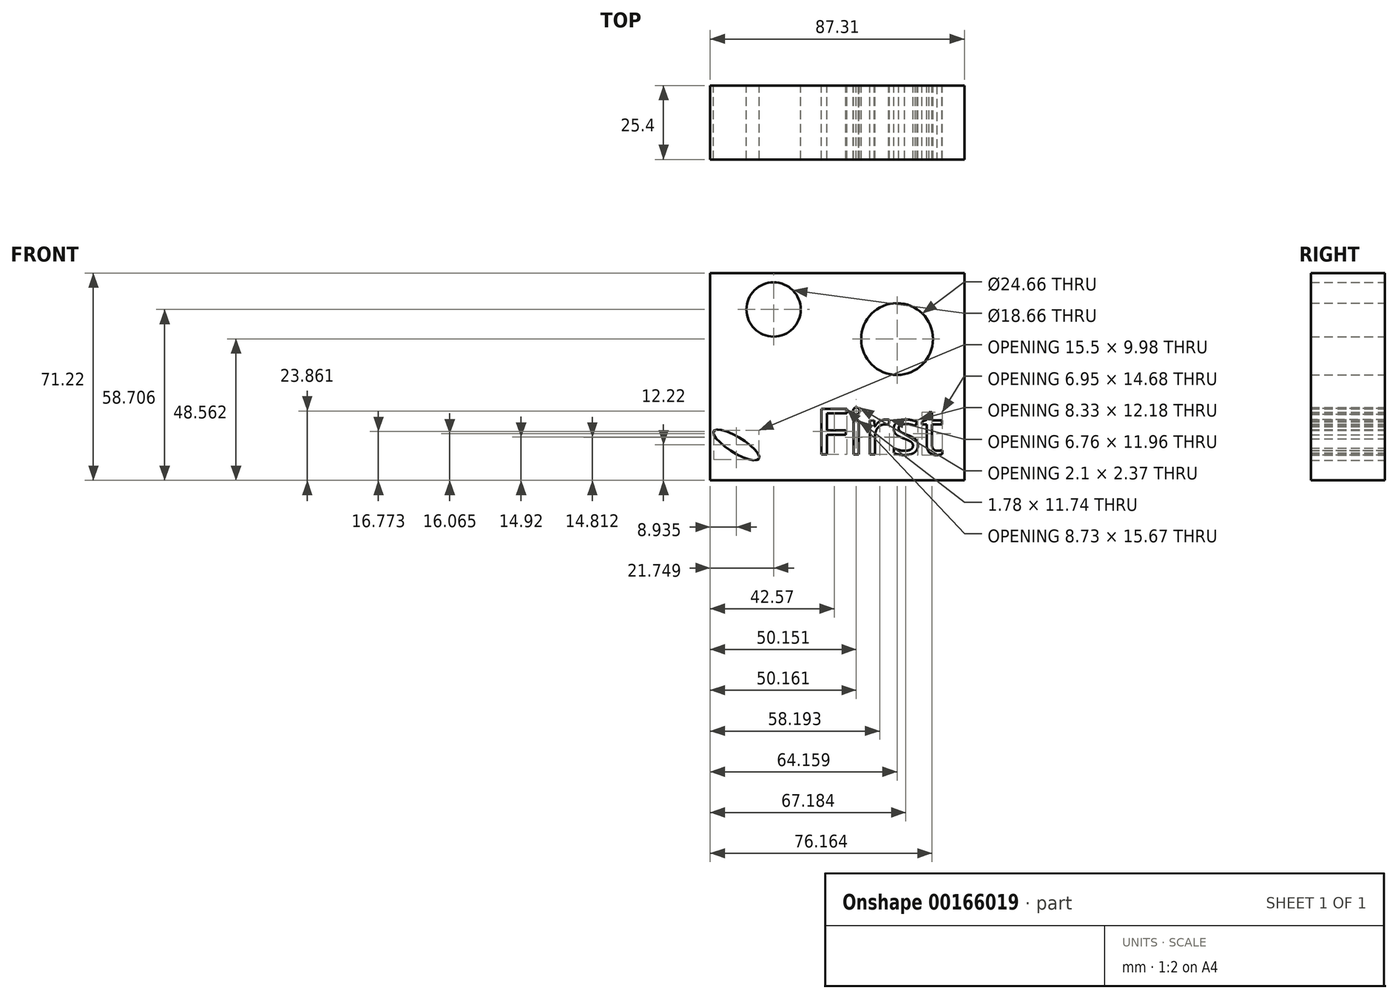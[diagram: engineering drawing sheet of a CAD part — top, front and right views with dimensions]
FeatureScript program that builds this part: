
annotation { "Feature Type Name" : "Feature", "Feature Type Description" : "" }
export const myFeature = defineFeature(function(context is Context, id is Id, definition is map)
    precondition{}
    {
        {
            var Q0;
            Q0=qCreatedBy(makeId("Front.planeOp"),FACE);
            var sketch = newSketch(context, id + "F0", { "sketchPlane" : qUnion([Q0])});
            skLineSegment(sketch, "E0", {"start": v(-43.8, 36.8) * mm, "end": v(43.5, 36.8) * mm});
            skLineSegment(sketch, "E1", {"start": v(43.5, 36.8) * mm, "end": v(43.5, -34.42) * mm});
            skLineSegment(sketch, "E2", {"start": v(43.5, -34.42) * mm, "end": v(-43.8, -34.42) * mm});
            skLineSegment(sketch, "E3", {"start": v(-43.8, -34.42) * mm, "end": v(-43.8, 36.8) * mm});
            skCircle(sketch, "E4", {"center": v(-22.05, 24.29) * mm, "radius": 9.33 * mm});
            skCircle(sketch, "E5", {"center": v(20.36, 14.14) * mm, "radius": 12.33 * mm});
            skPoint(sketch, "E5.first.point", {"position": v(11.03, 22.2) * mm});
            skPoint(sketch, "E5.second.point", {"position": v(30.4, 21.3) * mm});
            skPoint(sketch, "E5.third.point", {"position": v(31, 7.9) * mm});
            skEllipse(sketch, "E6", {"center": v(-34.86, -22.2) * mm, "majorRadius": 9.1 * mm, "minorRadius": 2.69 * mm, "majorAxis": v(0.85, -0.52)});
            skText(sketch, "E7", { "text": "First", "fontName": "OpenSans-Regular.ttf"});
            const initialGuessF0  = {"E7": [-0.00775, -0.02548, 1, 0, 0.0158]};
            skSetInitialGuess(sketch, initialGuessF0);
            skSolve(sketch);
        }
        {
            var Q0;
            Q0 = qSketchRegion(id + "F0", true);
            extrude(context, id + "F1", {"entities" : qUnion([Q0]), "depth" : 25.4 * mm});
        }
    });
